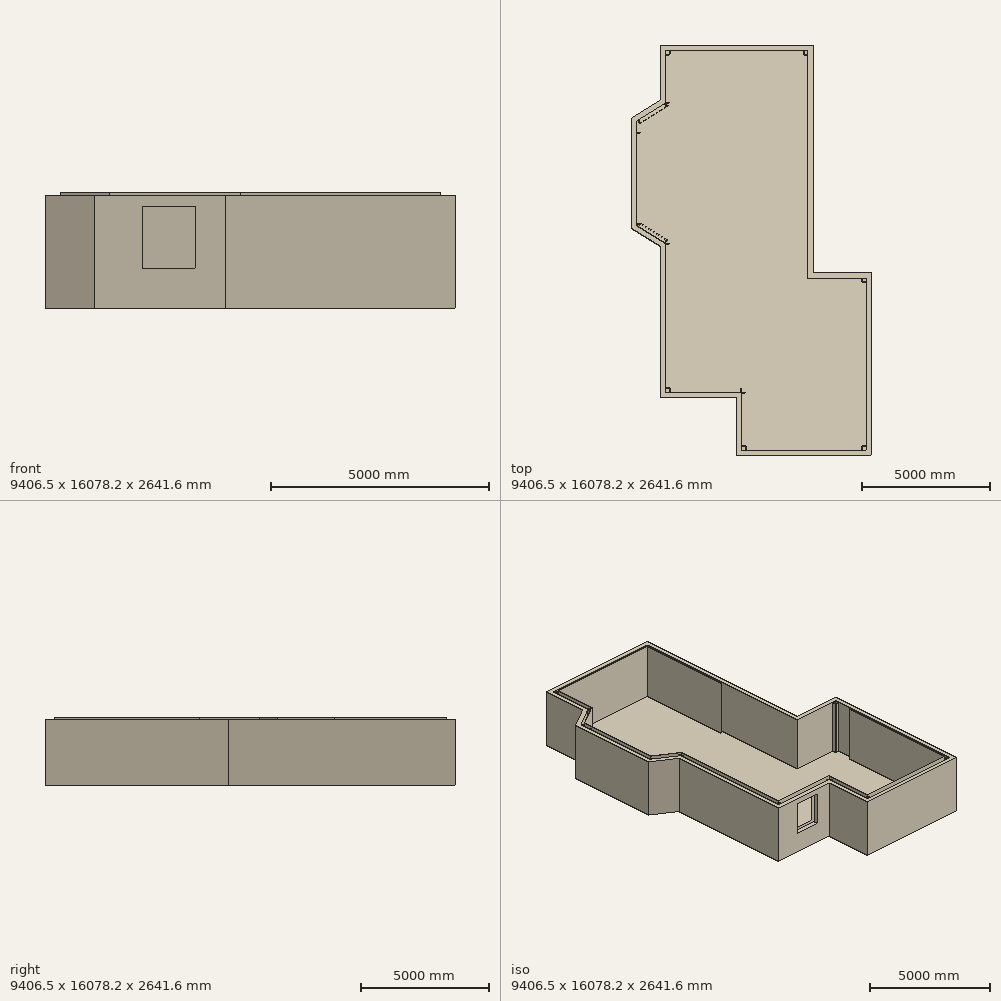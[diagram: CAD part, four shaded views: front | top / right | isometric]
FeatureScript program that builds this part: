
annotation { "Feature Type Name" : "Feature", "Feature Type Description" : "" }
export const myFeature = defineFeature(function(context is Context, id is Id, definition is map)
    precondition{}
    {
        {
            var Q0;
            Q0=qCreatedBy(makeId("Top.planeOp"),FACE);
            var sketch = newSketch(context, id + "F0", { "sketchPlane" : qUnion([Q0])});
            skLineSegment(sketch, "E0", {"start": v(-8280.4, 16078.2) * mm, "end": v(-2286, 16078.2) * mm});
            skLineSegment(sketch, "E1", {"start": v(-2286, 16078.2) * mm, "end": v(-2286, 7162.8) * mm});
            skLineSegment(sketch, "E2", {"start": v(-2286, 7162.8) * mm, "end": v(0, 7162.8) * mm});
            skLineSegment(sketch, "E3", {"start": v(0, 7162.8) * mm, "end": v(0, 0) * mm});
            skLineSegment(sketch, "E4", {"start": v(0, 0) * mm, "end": v(-5283.2, 0) * mm});
            skLineSegment(sketch, "E5", {"start": v(-5283.2, 0) * mm, "end": v(-5283.2, 2286) * mm});
            skLineSegment(sketch, "E6", {"start": v(-5283.2, 2286) * mm, "end": v(-8280.4, 2286) * mm});
            skLineSegment(sketch, "E7", {"start": v(-8280.4, 2286) * mm, "end": v(-8280.4, 8201.03) * mm});
            skLineSegment(sketch, "E8", {"start": v(-8280.4, 8201.03) * mm, "end": v(-9406.5, 8900.32) * mm});
            skLineSegment(sketch, "E9", {"start": v(-9406.5, 8900.32) * mm, "end": v(-9406.5, 13223.08) * mm});
            skLineSegment(sketch, "E10", {"start": v(-9406.5, 13223.08) * mm, "end": v(-8280.4, 13922.38) * mm});
            skLineSegment(sketch, "E11", {"start": v(-8280.4, 13922.38) * mm, "end": v(-8280.4, 16078.2) * mm});
            skSolve(sketch);
        }
        {
            var Q0;
            Q0=qSketchRegion(id+"F0",true);
            extrude(context, id + "F1", {"entities" : qUnion([Q0]), "depth" : 2578.1 * mm});
        }
        {
            var Q0;
            Q0=makeQuery(id+"F1.opExtrude","CAP_FACE",FACE,{"disambiguationData":[OSD([sQuery(id+"F0.wireOp",EDGE,"E0"),sQuery(id+"F0.wireOp",EDGE,"E1"),sQuery(id+"F0.wireOp",EDGE,"E2"),sQuery(id+"F0.wireOp",EDGE,"E3"),sQuery(id+"F0.wireOp",EDGE,"E4"),sQuery(id+"F0.wireOp",EDGE,"E5"),sQuery(id+"F0.wireOp",EDGE,"E6"),sQuery(id+"F0.wireOp",EDGE,"E7"),sQuery(id+"F0.wireOp",EDGE,"E8"),sQuery(id+"F0.wireOp",EDGE,"E9"),sQuery(id+"F0.wireOp",EDGE,"E10"),sQuery(id+"F0.wireOp",EDGE,"E11")])],"isStart":false});
            shell(context, id + "F2", {"entities" : qUnion([Q0]), "thickness" : 203.2 * mm});
        }
        {
            var Q0;
            Q0=makeQuery(id+"F2.opShell","OFFSET_FACE",FACE,{"disambiguationData":[OSD([sQuery(id+"F0.wireOp",EDGE,"E6")])]});
            var sketch = newSketch(context, id + "F3", { "sketchPlane" : qUnion([Q0])});
            skLineSegment(sketch, "E12.bottom", {"start": v(5969, 2324.1) * mm, "end": v(7188.2, 2324.1) * mm});
            skLineSegment(sketch, "E12.top", {"start": v(5969, 901.7) * mm, "end": v(7188.2, 901.7) * mm});
            skLineSegment(sketch, "E12.left", {"start": v(5969, 2324.1) * mm, "end": v(5969, 901.7) * mm});
            skLineSegment(sketch, "E12.right", {"start": v(7188.2, 2324.1) * mm, "end": v(7188.2, 901.7) * mm});
            skPoint(sketch, "E13", {"position": v(6578.6, 2324.1) * mm});
            skSolve(sketch);
        }
        {
            var Q0;
            Q0=makeQuery(id+"F2.opShell","OFFSET_FACE",FACE,{"disambiguationData":[OSD([sQuery(id+"F0.wireOp",EDGE,"E0"),sQuery(id+"F0.wireOp",EDGE,"E1"),sQuery(id+"F0.wireOp",EDGE,"E2"),sQuery(id+"F0.wireOp",EDGE,"E3"),sQuery(id+"F0.wireOp",EDGE,"E4"),sQuery(id+"F0.wireOp",EDGE,"E5"),sQuery(id+"F0.wireOp",EDGE,"E6"),sQuery(id+"F0.wireOp",EDGE,"E7"),sQuery(id+"F0.wireOp",EDGE,"E8"),sQuery(id+"F0.wireOp",EDGE,"E9"),sQuery(id+"F0.wireOp",EDGE,"E10"),sQuery(id+"F0.wireOp",EDGE,"E11")])]});
            var sketch = newSketch(context, id + "F4", { "sketchPlane" : qUnion([Q0])});
            skLineSegment(sketch, "E14.bottom", {"start": v(-8077.2, 13811.9) * mm, "end": v(-7937.5, 13811.9) * mm});
            skLineSegment(sketch, "E14.top", {"start": v(-8077.2, 13850) * mm, "end": v(-7937.5, 13850) * mm});
            skLineSegment(sketch, "E14.left", {"start": v(-8077.2, 13811.9) * mm, "end": v(-8077.2, 13850) * mm});
            skLineSegment(sketch, "E14.right", {"start": v(-7937.5, 13811.9) * mm, "end": v(-7937.5, 13850) * mm});
            skLineSegment(sketch, "E15.bottom", {"start": v(-7934.96, 15875) * mm, "end": v(-7896.86, 15875) * mm});
            skLineSegment(sketch, "E15.top", {"start": v(-7934.96, 15735.3) * mm, "end": v(-7896.86, 15735.3) * mm});
            skLineSegment(sketch, "E15.left", {"start": v(-7934.96, 15875) * mm, "end": v(-7934.96, 15735.3) * mm});
            skLineSegment(sketch, "E15.right", {"start": v(-7896.86, 15875) * mm, "end": v(-7896.86, 15735.3) * mm});
            skLineSegment(sketch, "E16.bottom", {"start": v(-8077.2, 15694.66) * mm, "end": v(-7937.5, 15694.66) * mm});
            skLineSegment(sketch, "E16.top", {"start": v(-8077.2, 15732.76) * mm, "end": v(-7937.5, 15732.76) * mm});
            skLineSegment(sketch, "E16.left", {"start": v(-8077.2, 15694.66) * mm, "end": v(-8077.2, 15732.76) * mm});
            skLineSegment(sketch, "E16.right", {"start": v(-7937.5, 15694.66) * mm, "end": v(-7937.5, 15732.76) * mm});
            skLineSegment(sketch, "E17.bottom", {"start": v(-2631.44, 15875) * mm, "end": v(-2669.54, 15875) * mm});
            skLineSegment(sketch, "E17.top", {"start": v(-2631.44, 15735.3) * mm, "end": v(-2669.54, 15735.3) * mm});
            skLineSegment(sketch, "E17.left", {"start": v(-2631.44, 15875) * mm, "end": v(-2631.44, 15735.3) * mm});
            skLineSegment(sketch, "E17.right", {"start": v(-2669.54, 15875) * mm, "end": v(-2669.54, 15735.3) * mm});
            skLineSegment(sketch, "E18.bottom", {"start": v(-2489.2, 15694.66) * mm, "end": v(-2628.9, 15694.66) * mm});
            skLineSegment(sketch, "E18.top", {"start": v(-2489.2, 15732.76) * mm, "end": v(-2628.9, 15732.76) * mm});
            skLineSegment(sketch, "E18.left", {"start": v(-2489.2, 15694.66) * mm, "end": v(-2489.2, 15732.76) * mm});
            skLineSegment(sketch, "E18.right", {"start": v(-2628.9, 15694.66) * mm, "end": v(-2628.9, 15732.76) * mm});
            skLineSegment(sketch, "E19", {"start": v(-8078.22, 13808.73) * mm, "end": v(-8110.59, 13788.64) * mm});
            skLineSegment(sketch, "E20", {"start": v(-8110.59, 13788.64) * mm, "end": v(-8036.89, 13669.96) * mm});
            skLineSegment(sketch, "E21", {"start": v(-8036.89, 13669.96) * mm, "end": v(-8004.52, 13690.06) * mm});
            skLineSegment(sketch, "E22", {"start": v(-8004.52, 13690.06) * mm, "end": v(-8078.22, 13808.73) * mm});
            skLineSegment(sketch, "E23.bottom", {"start": v(-9203.3, 12669.47) * mm, "end": v(-9063.6, 12669.47) * mm});
            skLineSegment(sketch, "E23.top", {"start": v(-9203.3, 12631.37) * mm, "end": v(-9063.6, 12631.37) * mm});
            skLineSegment(sketch, "E23.left", {"start": v(-9203.3, 12669.47) * mm, "end": v(-9203.3, 12631.37) * mm});
            skLineSegment(sketch, "E23.right", {"start": v(-9063.6, 12669.47) * mm, "end": v(-9063.6, 12631.37) * mm});
            skLineSegment(sketch, "E24", {"start": v(-9162.3, 13135.53) * mm, "end": v(-9129.94, 13155.63) * mm});
            skLineSegment(sketch, "E25", {"start": v(-9129.94, 13155.63) * mm, "end": v(-9056.24, 13036.95) * mm});
            skLineSegment(sketch, "E26", {"start": v(-9056.24, 13036.95) * mm, "end": v(-9088.6, 13016.85) * mm});
            skLineSegment(sketch, "E27", {"start": v(-9088.6, 13016.85) * mm, "end": v(-9162.3, 13135.53) * mm});
            skLineSegment(sketch, "E28", {"start": v(-9162.3, 8987.87) * mm, "end": v(-9088.6, 9106.55) * mm});
            skLineSegment(sketch, "E29", {"start": v(-9088.6, 9106.55) * mm, "end": v(-9056.24, 9086.45) * mm});
            skLineSegment(sketch, "E30", {"start": v(-9056.24, 9086.45) * mm, "end": v(-9129.94, 8967.77) * mm});
            skLineSegment(sketch, "E31", {"start": v(-9129.94, 8967.77) * mm, "end": v(-9162.3, 8987.87) * mm});
            skLineSegment(sketch, "E32", {"start": v(-8109.57, 8334.13) * mm, "end": v(-8077.2, 8314.03) * mm});
            skLineSegment(sketch, "E33", {"start": v(-8077.2, 8314.03) * mm, "end": v(-8003.5, 8432.71) * mm});
            skLineSegment(sketch, "E34", {"start": v(-8003.5, 8432.71) * mm, "end": v(-8035.87, 8452.81) * mm});
            skLineSegment(sketch, "E35", {"start": v(-8035.87, 8452.81) * mm, "end": v(-8109.57, 8334.13) * mm});
            skLineSegment(sketch, "E36.bottom", {"start": v(-9203.3, 9061.59) * mm, "end": v(-9063.6, 9061.59) * mm});
            skLineSegment(sketch, "E36.top", {"start": v(-9203.3, 9099.69) * mm, "end": v(-9063.6, 9099.69) * mm});
            skLineSegment(sketch, "E36.left", {"start": v(-9203.3, 9061.59) * mm, "end": v(-9203.3, 9099.69) * mm});
            skLineSegment(sketch, "E36.right", {"start": v(-9063.6, 9061.59) * mm, "end": v(-9063.6, 9099.69) * mm});
            skLineSegment(sketch, "E37.bottom", {"start": v(-8077.2, 8311.5) * mm, "end": v(-7937.5, 8311.5) * mm});
            skLineSegment(sketch, "E37.top", {"start": v(-8077.2, 8273.4) * mm, "end": v(-7937.5, 8273.4) * mm});
            skLineSegment(sketch, "E37.left", {"start": v(-8077.2, 8311.5) * mm, "end": v(-8077.2, 8273.4) * mm});
            skLineSegment(sketch, "E37.right", {"start": v(-7937.5, 8311.5) * mm, "end": v(-7937.5, 8273.4) * mm});
            skLineSegment(sketch, "E38.bottom", {"start": v(-8077.2, 2631.44) * mm, "end": v(-7937.5, 2631.44) * mm});
            skLineSegment(sketch, "E38.top", {"start": v(-8077.2, 2669.54) * mm, "end": v(-7937.5, 2669.54) * mm});
            skLineSegment(sketch, "E38.left", {"start": v(-8077.2, 2631.44) * mm, "end": v(-8077.2, 2669.54) * mm});
            skLineSegment(sketch, "E38.right", {"start": v(-7937.5, 2631.44) * mm, "end": v(-7937.5, 2669.54) * mm});
            skLineSegment(sketch, "E39.bottom", {"start": v(-7896.86, 2489.2) * mm, "end": v(-7934.96, 2489.2) * mm});
            skLineSegment(sketch, "E39.top", {"start": v(-7896.86, 2628.9) * mm, "end": v(-7934.96, 2628.9) * mm});
            skLineSegment(sketch, "E39.left", {"start": v(-7896.86, 2489.2) * mm, "end": v(-7896.86, 2628.9) * mm});
            skLineSegment(sketch, "E39.right", {"start": v(-7934.96, 2489.2) * mm, "end": v(-7934.96, 2628.9) * mm});
            skLineSegment(sketch, "E40.bottom", {"start": v(-5082.54, 2489.2) * mm, "end": v(-5120.64, 2489.2) * mm});
            skLineSegment(sketch, "E40.top", {"start": v(-5082.54, 2628.9) * mm, "end": v(-5120.64, 2628.9) * mm});
            skLineSegment(sketch, "E40.left", {"start": v(-5082.54, 2489.2) * mm, "end": v(-5082.54, 2628.9) * mm});
            skLineSegment(sketch, "E40.right", {"start": v(-5120.64, 2489.2) * mm, "end": v(-5120.64, 2628.9) * mm});
            skLineSegment(sketch, "E41.top", {"start": v(-5080, 2448.56) * mm, "end": v(-4940.3, 2448.56) * mm});
            skLineSegment(sketch, "E41.right", {"start": v(-4940.3, 2486.66) * mm, "end": v(-4940.3, 2448.56) * mm});
            skLineSegment(sketch, "E42.bottom", {"start": v(-5080, 345.44) * mm, "end": v(-4940.3, 345.44) * mm});
            skLineSegment(sketch, "E42.top", {"start": v(-5080, 383.54) * mm, "end": v(-4940.3, 383.54) * mm});
            skLineSegment(sketch, "E42.left", {"start": v(-5080, 345.44) * mm, "end": v(-5080, 383.54) * mm});
            skLineSegment(sketch, "E42.right", {"start": v(-4940.3, 345.44) * mm, "end": v(-4940.3, 383.54) * mm});
            skLineSegment(sketch, "E43.bottom", {"start": v(-4937.76, 203.2) * mm, "end": v(-4899.66, 203.2) * mm});
            skLineSegment(sketch, "E43.top", {"start": v(-4937.76, 342.9) * mm, "end": v(-4899.66, 342.9) * mm});
            skLineSegment(sketch, "E43.left", {"start": v(-4937.76, 203.2) * mm, "end": v(-4937.76, 342.9) * mm});
            skLineSegment(sketch, "E43.right", {"start": v(-4899.66, 203.2) * mm, "end": v(-4899.66, 342.9) * mm});
            skLineSegment(sketch, "E44.bottom", {"start": v(-383.54, 203.2) * mm, "end": v(-345.44, 203.2) * mm});
            skLineSegment(sketch, "E44.top", {"start": v(-383.54, 342.9) * mm, "end": v(-345.44, 342.9) * mm});
            skLineSegment(sketch, "E44.left", {"start": v(-383.54, 203.2) * mm, "end": v(-383.54, 342.9) * mm});
            skLineSegment(sketch, "E44.right", {"start": v(-345.44, 203.2) * mm, "end": v(-345.44, 342.9) * mm});
            skLineSegment(sketch, "E45.bottom", {"start": v(-203.2, 345.44) * mm, "end": v(-342.9, 345.44) * mm});
            skLineSegment(sketch, "E45.top", {"start": v(-203.2, 383.54) * mm, "end": v(-342.9, 383.54) * mm});
            skLineSegment(sketch, "E45.left", {"start": v(-203.2, 345.44) * mm, "end": v(-203.2, 383.54) * mm});
            skLineSegment(sketch, "E45.right", {"start": v(-342.9, 345.44) * mm, "end": v(-342.9, 383.54) * mm});
            skLineSegment(sketch, "E46.bottom", {"start": v(-203.2, 6779.26) * mm, "end": v(-342.9, 6779.26) * mm});
            skLineSegment(sketch, "E46.top", {"start": v(-203.2, 6817.36) * mm, "end": v(-342.9, 6817.36) * mm});
            skLineSegment(sketch, "E46.left", {"start": v(-203.2, 6779.26) * mm, "end": v(-203.2, 6817.36) * mm});
            skLineSegment(sketch, "E46.right", {"start": v(-342.9, 6779.26) * mm, "end": v(-342.9, 6817.36) * mm});
            skLineSegment(sketch, "E47.bottom", {"start": v(-345.44, 6959.6) * mm, "end": v(-383.54, 6959.6) * mm});
            skLineSegment(sketch, "E47.top", {"start": v(-345.44, 6819.9) * mm, "end": v(-383.54, 6819.9) * mm});
            skLineSegment(sketch, "E47.left", {"start": v(-345.44, 6959.6) * mm, "end": v(-345.44, 6819.9) * mm});
            skLineSegment(sketch, "E47.right", {"start": v(-383.54, 6959.6) * mm, "end": v(-383.54, 6819.9) * mm});
            skLineSegment(sketch, "E48", {"start": v(-4940.3, 2486.66) * mm, "end": v(-5080, 2486.66) * mm});
            skLineSegment(sketch, "E49", {"start": v(-5080, 2486.66) * mm, "end": v(-5080, 2448.56) * mm});
            skLineSegment(sketch, "E50", {"start": v(-9203.3, 13110.07) * mm, "end": v(-9045.7, 12987.43) * mm, "construction": true});
            skLineSegment(sketch, "E51", {"start": v(-9045.7, 12987.43) * mm, "end": v(-9104.83, 13171.22) * mm, "construction": true});
            skLineSegment(sketch, "E52", {"start": v(-9104.83, 13171.22) * mm, "end": v(-9203.3, 12968.55) * mm, "construction": true});
            skLineSegment(sketch, "E53", {"start": v(-9203.3, 12968.55) * mm, "end": v(-9045.7, 12987.43) * mm, "construction": true});
            skSolve(sketch);
        }
        {
            var Q0;
            Q0=qSketchRegion(id+"F3",true);
            var Q1;
            Q1=makeQuery(id+"FwcOo8eikqoZCvb_1.opExtrude","SWEPT_FACE",FACE,{"disambiguationData":[OSD([sQuery(id+"F7.wireOp",EDGE,"E55.top"),sQuery(id+"F7.wireOp",EDGE,"E63")])]});
            extrude(context, id + "F5", {"entities" : qUnion([Q0]), "operationType" : NewBodyOperationType.REMOVE, "endBound" : BoundingType.UP_TO_NEXT, "oppositeDirection" : true, "depth" : 25.4 * mm});
        }
        {
            var Q0;
            Q0=qSketchRegion(id+"F4",true);
            extrude(context, id + "F6", {"entities" : qUnion([Q0]), "operationType" : NewBodyOperationType.ADD, "depth" : 2349.5 * mm});
        }
        {
            var Q0;
            Q0=makeQuery(id+"F2.opShell","OFFSET_FACE",FACE,{"disambiguationData":[OSD([sQuery(id+"F0.wireOp",EDGE,"E0"),sQuery(id+"F0.wireOp",EDGE,"E1"),sQuery(id+"F0.wireOp",EDGE,"E2"),sQuery(id+"F0.wireOp",EDGE,"E3"),sQuery(id+"F0.wireOp",EDGE,"E4"),sQuery(id+"F0.wireOp",EDGE,"E5"),sQuery(id+"F0.wireOp",EDGE,"E6"),sQuery(id+"F0.wireOp",EDGE,"E7"),sQuery(id+"F0.wireOp",EDGE,"E8"),sQuery(id+"F0.wireOp",EDGE,"E9"),sQuery(id+"F0.wireOp",EDGE,"E10"),sQuery(id+"F0.wireOp",EDGE,"E11")])]});
            var sketch = newSketch(context, id + "F7", { "sketchPlane" : qUnion([Q0])});
            skLineSegment(sketch, "E54.bottom", {"start": v(-7937.5, 8391.73) * mm, "end": v(-7924.8, 8391.73) * mm, "construction": true});
            skLineSegment(sketch, "E54.top", {"start": v(-7937.5, 2641.6) * mm, "end": v(-7924.8, 2641.6) * mm, "construction": true});
            skLineSegment(sketch, "E54.left", {"start": v(-7937.5, 8391.73) * mm, "end": v(-7937.5, 2641.6) * mm});
            skLineSegment(sketch, "E54.right", {"start": v(-7924.8, 8391.73) * mm, "end": v(-7924.8, 2641.6) * mm});
            skLineSegment(sketch, "E55.bottom", {"start": v(-7924.8, 2628.9) * mm, "end": v(-4940.3, 2628.9) * mm});
            skLineSegment(sketch, "E55.top", {"start": v(-7924.8, 2641.6) * mm, "end": v(-4940.3, 2641.6) * mm});
            skLineSegment(sketch, "E55.left", {"start": v(-7924.8, 2628.9) * mm, "end": v(-7924.8, 2641.6) * mm, "construction": true});
            skLineSegment(sketch, "E55.right", {"start": v(-4940.3, 2628.9) * mm, "end": v(-4940.3, 2641.6) * mm, "construction": true});
            skLineSegment(sketch, "E56", {"start": v(-7924.8, 2628.9) * mm, "end": v(-7937.5, 2628.9) * mm});
            skLineSegment(sketch, "E57", {"start": v(-7937.5, 2628.9) * mm, "end": v(-7937.5, 2641.6) * mm});
            skLineSegment(sketch, "E58.bottom", {"start": v(-4940.3, 2628.9) * mm, "end": v(-4927.6, 2628.9) * mm, "construction": true});
            skLineSegment(sketch, "E58.top", {"start": v(-4940.3, 355.6) * mm, "end": v(-4927.6, 355.6) * mm, "construction": true});
            skLineSegment(sketch, "E58.left", {"start": v(-4940.3, 2628.9) * mm, "end": v(-4940.3, 355.6) * mm});
            skLineSegment(sketch, "E58.right", {"start": v(-4927.6, 2628.9) * mm, "end": v(-4927.6, 355.6) * mm});
            skLineSegment(sketch, "E59.bottom", {"start": v(-4927.6, 342.9) * mm, "end": v(-355.6, 342.9) * mm});
            skLineSegment(sketch, "E59.top", {"start": v(-4927.6, 355.6) * mm, "end": v(-355.6, 355.6) * mm});
            skLineSegment(sketch, "E59.left", {"start": v(-4927.6, 342.9) * mm, "end": v(-4927.6, 355.6) * mm, "construction": true});
            skLineSegment(sketch, "E59.right", {"start": v(-355.6, 342.9) * mm, "end": v(-355.6, 355.6) * mm, "construction": true});
            skLineSegment(sketch, "E60", {"start": v(-4940.3, 355.6) * mm, "end": v(-4940.3, 342.9) * mm});
            skLineSegment(sketch, "E61", {"start": v(-4940.3, 342.9) * mm, "end": v(-4927.6, 342.9) * mm});
            skLineSegment(sketch, "E62", {"start": v(-4927.6, 2628.9) * mm, "end": v(-4927.6, 2641.6) * mm});
            skLineSegment(sketch, "E63", {"start": v(-4940.3, 2641.6) * mm, "end": v(-4927.6, 2641.6) * mm});
            skLineSegment(sketch, "E64.bottom", {"start": v(-355.6, 355.6) * mm, "end": v(-342.9, 355.6) * mm, "construction": true});
            skLineSegment(sketch, "E64.top", {"start": v(-355.6, 6019.58) * mm, "end": v(-342.9, 6019.58) * mm});
            skLineSegment(sketch, "E64.left", {"start": v(-355.6, 355.6) * mm, "end": v(-355.6, 6019.58) * mm});
            skLineSegment(sketch, "E64.right", {"start": v(-342.9, 355.6) * mm, "end": v(-342.9, 6019.58) * mm});
            skLineSegment(sketch, "E65", {"start": v(-355.6, 342.9) * mm, "end": v(-342.9, 342.9) * mm});
            skLineSegment(sketch, "E66", {"start": v(-342.9, 342.9) * mm, "end": v(-342.9, 355.6) * mm});
            skLineSegment(sketch, "E67", {"start": v(-7937.5, 8391.73) * mm, "end": v(-9063.6, 9091.02) * mm});
            skLineSegment(sketch, "E68", {"start": v(-9063.6, 9091.02) * mm, "end": v(-9063.6, 13032.38) * mm});
            skLineSegment(sketch, "E69", {"start": v(-9063.6, 13032.38) * mm, "end": v(-7937.5, 13731.67) * mm});
            skLineSegment(sketch, "E70", {"start": v(-7937.5, 13731.67) * mm, "end": v(-7937.5, 15735.3) * mm});
            skLineSegment(sketch, "E71", {"start": v(-7937.5, 15735.3) * mm, "end": v(-2628.9, 15735.3) * mm});
            skLineSegment(sketch, "E72", {"start": v(-2628.9, 15735.3) * mm, "end": v(-2628.9, 11339.58) * mm});
            skLineSegment(sketch, "E73", {"start": v(-2628.9, 11339.58) * mm, "end": v(-2641.6, 11339.58) * mm});
            skLineSegment(sketch, "E74", {"start": v(-2641.6, 11339.58) * mm, "end": v(-2641.6, 15722.6) * mm});
            skLineSegment(sketch, "E75", {"start": v(-2641.6, 15722.6) * mm, "end": v(-7924.8, 15722.6) * mm});
            skLineSegment(sketch, "E76", {"start": v(-7924.8, 15722.6) * mm, "end": v(-7924.8, 13724.61) * mm});
            skLineSegment(sketch, "E77", {"start": v(-7924.8, 13724.61) * mm, "end": v(-9050.9, 13025.32) * mm});
            skLineSegment(sketch, "E78", {"start": v(-9050.9, 13025.32) * mm, "end": v(-9050.9, 9098.08) * mm});
            skLineSegment(sketch, "E79", {"start": v(-9050.9, 9098.08) * mm, "end": v(-7924.8, 8398.79) * mm});
            skLineSegment(sketch, "E80", {"start": v(-8493.85, 8752.16) * mm, "end": v(-8500.55, 8741.37) * mm, "construction": true});
            skLineSegment(sketch, "E81", {"start": v(-9063.6, 11061.7) * mm, "end": v(-9050.9, 11061.7) * mm, "construction": true});
            skLineSegment(sketch, "E82", {"start": v(-8487.85, 13374.97) * mm, "end": v(-8494.55, 13385.75) * mm, "construction": true});
            skLineSegment(sketch, "E83", {"start": v(-7924.8, 15722.6) * mm, "end": v(-7937.5, 15722.6) * mm, "construction": true});
            skLineSegment(sketch, "E84", {"start": v(-2641.6, 15735.3) * mm, "end": v(-2641.6, 15722.6) * mm, "construction": true});
            skLineSegment(sketch, "E85", {"start": v(-7924.8, 8391.73) * mm, "end": v(-7924.8, 8398.79) * mm});
            skSolve(sketch);
        }
        {
            var Q0;
            Q0=qSketchRegion(id+"F7",true);
            extrude(context, id + "F8", {"entities" : qUnion([Q0]), "depth" : 12 * 203.2 * mm});
        }
        {
            var Q0;
            Q0=qSketchRegion(id+"F3",true);
            var Q1;
            Q1=makeQuery(id+"F8.opExtrude","SWEPT_FACE",FACE,{"disambiguationData":[OSD([sQuery(id+"F7.wireOp",EDGE,"E55.top"),sQuery(id+"F7.wireOp",EDGE,"E63")])]});
            extrude(context, id + "F9", {"entities" : qUnion([Q0]), "operationType" : NewBodyOperationType.REMOVE, "endBound" : BoundingType.UP_TO_SURFACE, "endBoundEntityFace" : qUnion([Q1]), "depth" : 25.4 * mm});
        }
        {
            var Q0;
            Q0=qCreatedBy(makeId("Top.planeOp"),FACE);
            var sketch = newSketch(context, id + "F10", { "sketchPlane" : qUnion([Q0])});
            skLineSegment(sketch, "E86", {"start": v(-8077.2, 2489.2) * mm, "end": v(-8077.2, 8314.03) * mm});
            skLineSegment(sketch, "E87", {"start": v(-8077.2, 8314.03) * mm, "end": v(-9203.3, 9013.33) * mm});
            skLineSegment(sketch, "E88", {"start": v(-9203.3, 9013.33) * mm, "end": v(-9203.3, 13110.07) * mm});
            skLineSegment(sketch, "E89", {"start": v(-9203.3, 13110.07) * mm, "end": v(-8077.2, 13809.37) * mm});
            skLineSegment(sketch, "E90", {"start": v(-8077.2, 13809.37) * mm, "end": v(-8077.2, 15875) * mm});
            skLineSegment(sketch, "E91", {"start": v(-8077.2, 15875) * mm, "end": v(-2489.2, 15875) * mm});
            skLineSegment(sketch, "E92", {"start": v(-2489.2, 15875) * mm, "end": v(-2489.2, 11339.58) * mm});
            skLineSegment(sketch, "E93", {"start": v(-2489.2, 11339.58) * mm, "end": v(-2628.9, 11339.58) * mm});
            skLineSegment(sketch, "E94", {"start": v(-2628.9, 11339.58) * mm, "end": v(-2628.9, 15735.3) * mm});
            skLineSegment(sketch, "E95", {"start": v(-7937.5, 15735.3) * mm, "end": v(-7937.5, 13731.67) * mm});
            skLineSegment(sketch, "E96", {"start": v(-7937.5, 13731.67) * mm, "end": v(-9063.6, 13032.38) * mm});
            skLineSegment(sketch, "E97", {"start": v(-9063.6, 13032.38) * mm, "end": v(-9063.6, 9091.02) * mm});
            skLineSegment(sketch, "E98", {"start": v(-9063.6, 9091.02) * mm, "end": v(-7937.5, 8391.73) * mm});
            skLineSegment(sketch, "E99", {"start": v(-7937.5, 8391.73) * mm, "end": v(-7937.5, 2628.9) * mm});
            skLineSegment(sketch, "E100", {"start": v(-7937.5, 2628.9) * mm, "end": v(-4940.3, 2628.9) * mm});
            skLineSegment(sketch, "E101", {"start": v(-4940.3, 2628.9) * mm, "end": v(-4940.3, 342.9) * mm});
            skLineSegment(sketch, "E102", {"start": v(-4940.3, 342.9) * mm, "end": v(-342.9, 342.9) * mm});
            skLineSegment(sketch, "E103", {"start": v(-342.9, 342.9) * mm, "end": v(-342.9, 5526.42) * mm});
            skLineSegment(sketch, "E104", {"start": v(-342.9, 5526.42) * mm, "end": v(-203.2, 5526.42) * mm});
            skLineSegment(sketch, "E105", {"start": v(-203.2, 5526.42) * mm, "end": v(-203.2, 203.2) * mm});
            skLineSegment(sketch, "E106", {"start": v(-203.2, 203.2) * mm, "end": v(-5080, 203.2) * mm});
            skLineSegment(sketch, "E107", {"start": v(-5080, 203.2) * mm, "end": v(-5080, 2489.2) * mm});
            skLineSegment(sketch, "E108", {"start": v(-5080, 2489.2) * mm, "end": v(-8077.2, 2489.2) * mm});
            skLineSegment(sketch, "E109", {"start": v(-9203.3, 11061.7) * mm, "end": v(-9063.6, 11061.7) * mm, "construction": true});
            skLineSegment(sketch, "E110", {"start": v(-8566.55, 13341.04) * mm, "end": v(-8640.25, 13459.72) * mm, "construction": true});
            skLineSegment(sketch, "E111", {"start": v(-8077.2, 14842.18) * mm, "end": v(-7937.5, 14842.18) * mm, "construction": true});
            skLineSegment(sketch, "E112", {"start": v(-2489.2, 13607.29) * mm, "end": v(-2628.9, 13607.29) * mm, "construction": true});
            skLineSegment(sketch, "E113", {"start": v(-7937.5, 15735.3) * mm, "end": v(-2628.9, 15735.3) * mm});
            skLineSegment(sketch, "E114", {"start": v(-5283.2, 15735.3) * mm, "end": v(-5283.2, 15875) * mm, "construction": true});
            skLineSegment(sketch, "E115", {"start": v(-8640.25, 8663.68) * mm, "end": v(-8566.55, 8782.36) * mm, "construction": true});
            skLineSegment(sketch, "E116", {"start": v(-7937.5, 5401.62) * mm, "end": v(-8077.2, 5401.62) * mm, "construction": true});
            skLineSegment(sketch, "E117", {"start": v(-6578.6, 2489.2) * mm, "end": v(-6578.6, 2628.9) * mm, "construction": true});
            skSolve(sketch);
        }
        {
            var Q0;
            Q0=qSketchRegion(id+"F10",true);
            extrude(context, id + "F11", {"entities" : qUnion([Q0]), "depth" : 12.7 * mm});
        }
    });
